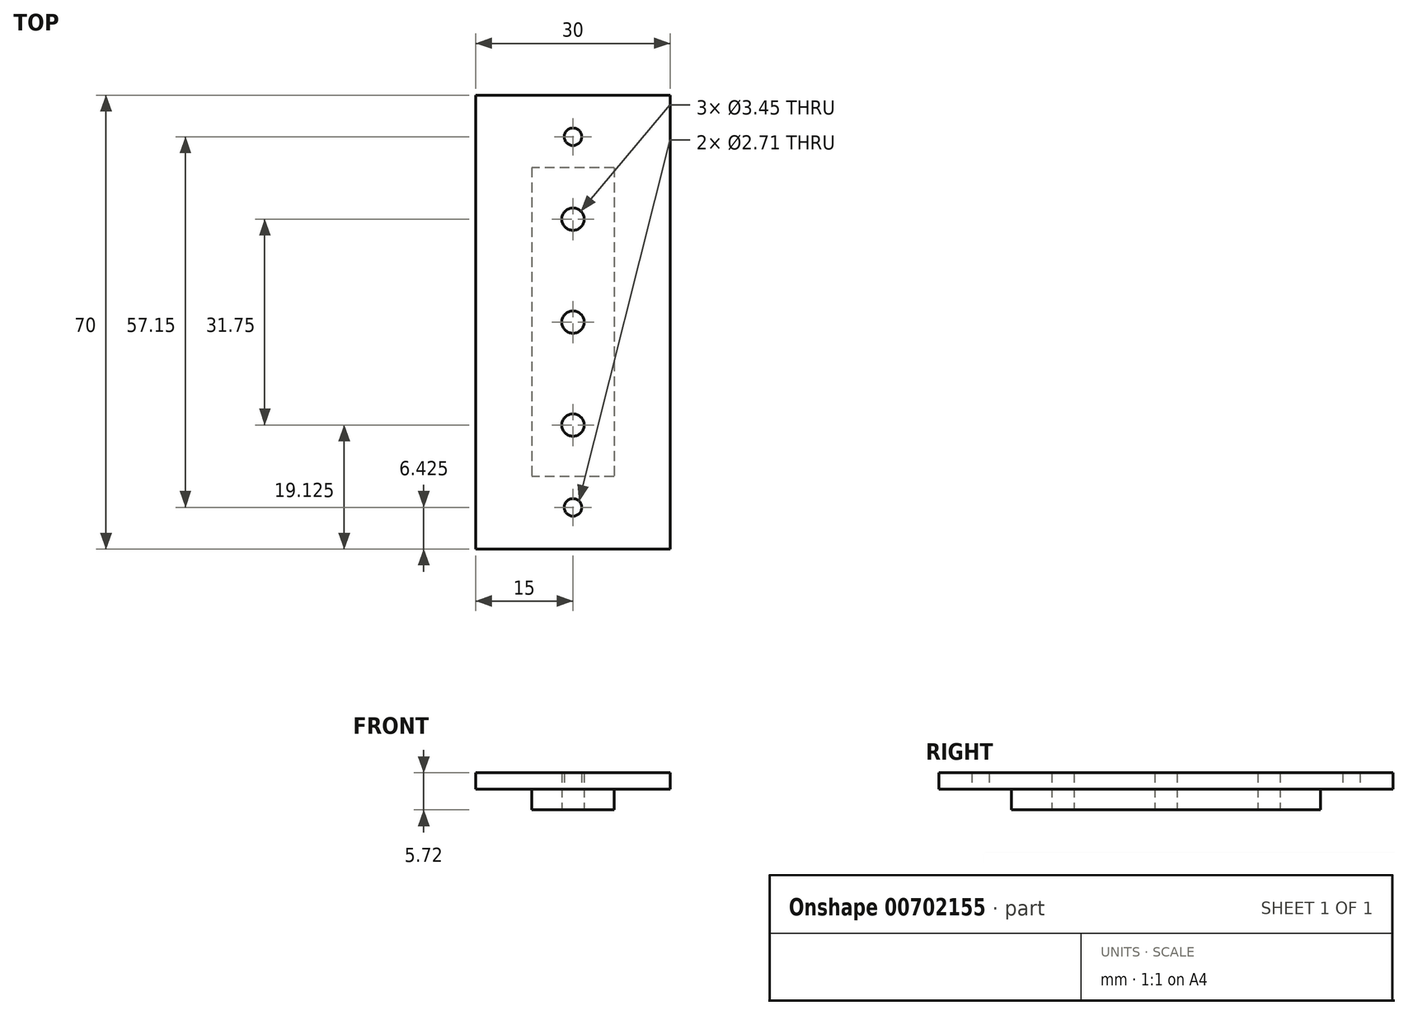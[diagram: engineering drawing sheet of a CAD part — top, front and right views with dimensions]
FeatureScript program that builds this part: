
annotation { "Feature Type Name" : "Feature", "Feature Type Description" : "" }
export const myFeature = defineFeature(function(context is Context, id is Id, definition is map)
    precondition{}
    {
        {
            var Q0;
            Q0=qCreatedBy(makeId("Top.planeOp"),FACE);
            var sketch = newSketch(context, id + "F0", { "sketchPlane" : qUnion([Q0])});
            skLineSegment(sketch, "E0.bottom", {"start": v(6.35, 23.81) * mm, "end": v(-6.35, 23.81) * mm});
            skLineSegment(sketch, "E0.top", {"start": v(6.35, -23.81) * mm, "end": v(-6.35, -23.81) * mm});
            skLineSegment(sketch, "E0.left", {"start": v(6.35, 23.81) * mm, "end": v(6.35, -23.81) * mm});
            skLineSegment(sketch, "E0.right", {"start": v(-6.35, 23.81) * mm, "end": v(-6.35, -23.81) * mm});
            skPoint(sketch, "E0.middle", {"position": v(0, 0) * mm});
            skSolve(sketch);
        }
        {
            var Q0;
            Q0=makeQuery(id+"F0.imprint","IMPRINT",FACE,{"disambiguationData":[TD([[makeQuery(id+"F0.imprint","IMPRINT",EDGE,{"derivedFrom":sQuery(id+"F0.wireOp",EDGE,"E0.bottom")}),1.0]])]});
            extrude(context, id + "F1", {"entities" : qUnion([Q0]), "depth" : 3.17 * mm, "offsetDistance" : 25.4 * mm});
        }
        {
            var Q0;
            Q0=makeQuery(id+"F1.opExtrude","CAP_FACE",FACE,{"disambiguationData":[OSD([sQuery(id+"F0.wireOp",EDGE,"E0.bottom"),sQuery(id+"F0.wireOp",EDGE,"E0.top"),sQuery(id+"F0.wireOp",EDGE,"E0.left"),sQuery(id+"F0.wireOp",EDGE,"E0.right")])],"isStart":false});
            var sketch = newSketch(context, id + "F2", { "sketchPlane" : qUnion([Q0])});
            skLineSegment(sketch, "E1.bottom", {"start": v(15, -35) * mm, "end": v(-15, -35) * mm});
            skLineSegment(sketch, "E1.top", {"start": v(15, 35) * mm, "end": v(-15, 35) * mm});
            skLineSegment(sketch, "E1.left", {"start": v(15, -35) * mm, "end": v(15, 35) * mm});
            skLineSegment(sketch, "E1.right", {"start": v(-15, -35) * mm, "end": v(-15, 35) * mm});
            skPoint(sketch, "E1.middle", {"position": v(0, 0) * mm});
            skSolve(sketch);
        }
        {
            var Q0;
            Q0 = qSketchRegion(id + "F2", true);
            extrude(context, id + "F3", {"entities" : qUnion([Q0]), "operationType" : NewBodyOperationType.ADD, "depth" : 2.54 * mm, "offsetDistance" : 25.4 * mm});
        }
        {
            var Q0;
            Q0=makeQuery(id+"F1.opExtrude","CAP_FACE",FACE,{"disambiguationData":[OSD([sQuery(id+"F0.wireOp",EDGE,"E0.bottom"),sQuery(id+"F0.wireOp",EDGE,"E0.top"),sQuery(id+"F0.wireOp",EDGE,"E0.left"),sQuery(id+"F0.wireOp",EDGE,"E0.right")])],"isStart":true});
            var sketch = newSketch(context, id + "F4", { "sketchPlane" : qUnion([Q0])});
            skLineSegment(sketch, "E2", {"start": v(0, 0) * mm, "end": v(0, 15.88) * mm});
            skLineSegment(sketch, "E3", {"start": v(0, 0) * mm, "end": v(0, -15.88) * mm});
            skLineSegment(sketch, "E4.bottom", {"start": v(4.76, 20.64) * mm, "end": v(-4.76, 20.64) * mm, "construction": true});
            skLineSegment(sketch, "E4.top", {"start": v(4.76, 11.11) * mm, "end": v(-4.76, 11.11) * mm, "construction": true});
            skLineSegment(sketch, "E4.left", {"start": v(4.76, 20.64) * mm, "end": v(4.76, 11.11) * mm, "construction": true});
            skLineSegment(sketch, "E4.right", {"start": v(-4.76, 20.64) * mm, "end": v(-4.76, 11.11) * mm, "construction": true});
            skPoint(sketch, "E4.middle", {"position": v(0, 15.88) * mm});
            skSolve(sketch);
        }
        {
            var Q0;
            Q0=sQuery(id+"F4.wireOp",VERTEX,"E4.middle");
            var Q1;
            Q1=sQuery(id+"F4.wireOp",VERTEX,"E3.start");
            var Q2;
            Q2=sQuery(id+"F4.wireOp",VERTEX,"E3.end");
            var Q3;
            Q3=makeQuery(id+"F1.opExtrude","SWEPT_BODY",BODY,{"disambiguationData":[OSD([sQuery(id+"F0.wireOp",EDGE,"E0.bottom"),sQuery(id+"F0.wireOp",EDGE,"E0.top"),sQuery(id+"F0.wireOp",EDGE,"E0.left"),sQuery(id+"F0.wireOp",EDGE,"E0.right")])]});
            hole(context, id + "F5", {"style" : HoleStyle.SIMPLE, "endStyle" : HoleEndStyle.BLIND, "standardTappedOrClearance" : lookupTablePath({ "standard" : "ANSI", "engagement" : "75%", "pitch" : "32 tpi", "size" : "#8", "type" : "Tapped" }), "standardBlindInLast" : lookupTablePath({ "standard" : "ANSI", "engagement" : "75%", "pitch" : "32 tpi", "size" : "#8", "type" : "Tapped" }), "holeDiameter" : 3.45 * mm, "majorDiameter" : 4.17 * mm, "showTappedDepth" : true, "holeDepth" : 15.08 * mm, "isTappedThrough" : true, "tappedDepth" : 12.7 * mm, "tapClearance" : 3, "locations" : qUnion([Q0, Q1, Q2]), "scope" : qUnion([Q3])});
        }
        {
            var Q0;
            Q0=makeQuery(id+"F3.opExtrude","CAP_FACE",FACE,{"disambiguationData":[OSD([sQuery(id+"F2.wireOp",EDGE,"E1.bottom"),sQuery(id+"F2.wireOp",EDGE,"E1.top"),sQuery(id+"F2.wireOp",EDGE,"E1.left"),sQuery(id+"F2.wireOp",EDGE,"E1.right")])],"isStart":true});
            var sketch = newSketch(context, id + "F6", { "sketchPlane" : qUnion([Q0])});
            skLineSegment(sketch, "E5", {"start": v(0, 0) * mm, "end": v(0, 28.58) * mm});
            skPoint(sketch, "E5.endSnap0", {"position": v(0, 23.81) * mm});
            skLineSegment(sketch, "E6", {"start": v(0, 0) * mm, "end": v(0, -28.58) * mm});
            skSolve(sketch);
        }
        {
            var Q0;
            Q0=sQuery(id+"F6.wireOp",VERTEX,"E5.end");
            var Q1;
            Q1=sQuery(id+"F6.wireOp",VERTEX,"E6.end");
            var Q2;
            Q2=makeQuery(id+"F1.opExtrude","SWEPT_BODY",BODY,{"disambiguationData":[OSD([sQuery(id+"F0.wireOp",EDGE,"E0.bottom"),sQuery(id+"F0.wireOp",EDGE,"E0.top"),sQuery(id+"F0.wireOp",EDGE,"E0.left"),sQuery(id+"F0.wireOp",EDGE,"E0.right")])]});
            hole(context, id + "F7", {"style" : HoleStyle.SIMPLE, "endStyle" : HoleEndStyle.BLIND, "standardTappedOrClearance" : lookupTablePath({ "standard" : "ANSI", "engagement" : "75%", "pitch" : "32 tpi", "size" : "#6", "type" : "Tapped" }), "standardBlindInLast" : lookupTablePath({ "standard" : "ANSI", "engagement" : "75%", "pitch" : "32 tpi", "size" : "#6", "type" : "Tapped" }), "holeDiameter" : 2.7 * mm, "majorDiameter" : 3.5 * mm, "showTappedDepth" : true, "holeDepth" : 15.1 * mm, "isTappedThrough" : true, "tappedDepth" : 12.7 * mm, "tapClearance" : 3, "locations" : qUnion([Q0, Q1]), "scope" : qUnion([Q2])});
        }
    });
